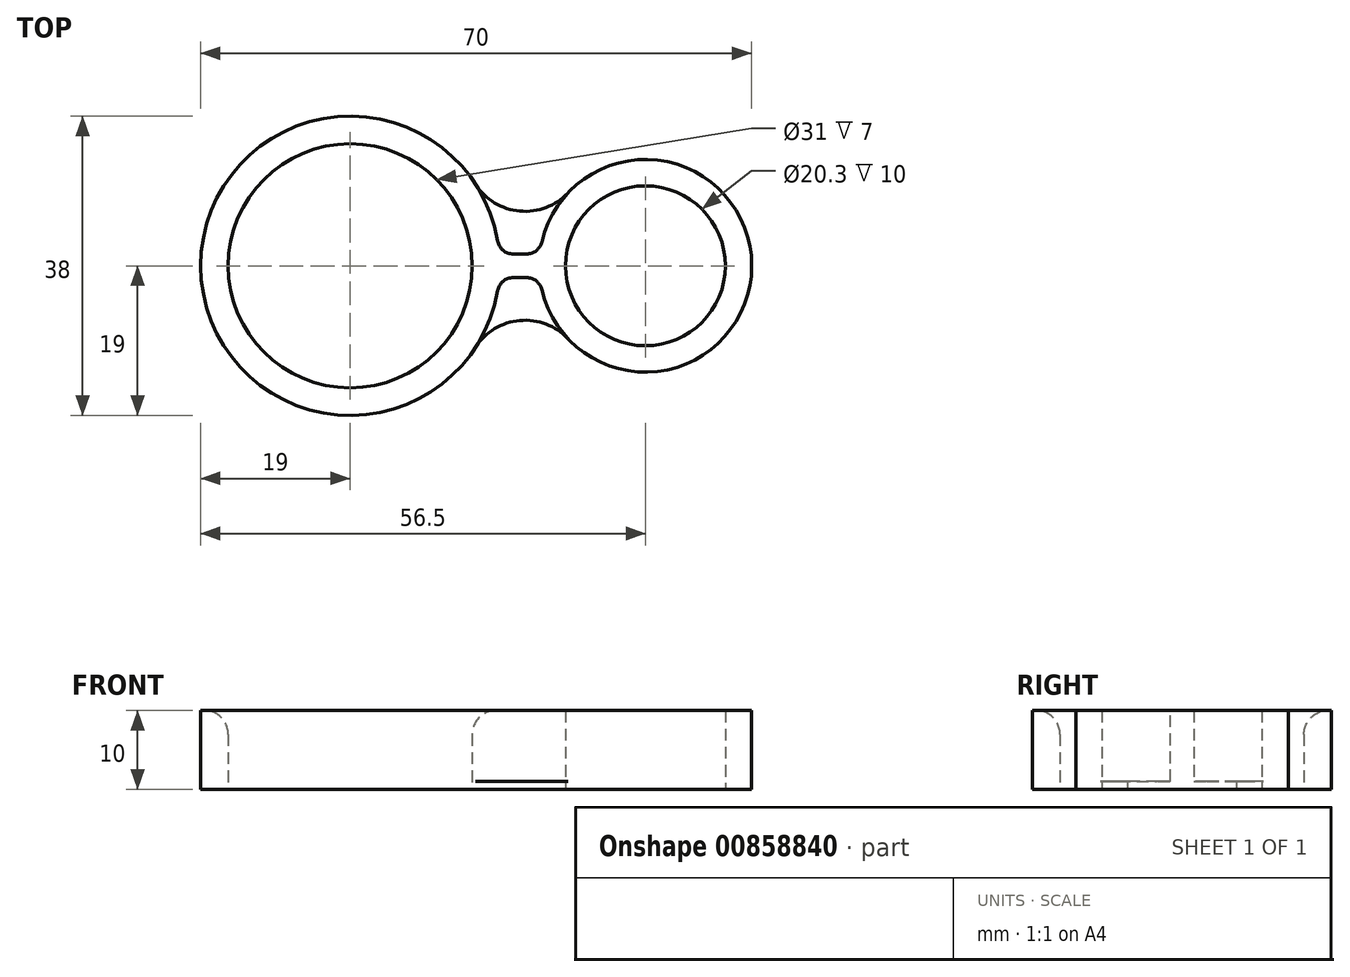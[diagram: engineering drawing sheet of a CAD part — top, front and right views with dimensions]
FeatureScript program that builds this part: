
annotation { "Feature Type Name" : "Feature", "Feature Type Description" : "" }
export const myFeature = defineFeature(function(context is Context, id is Id, definition is map)
    precondition{}
    {
        {
            var Q0;
            Q0=qCreatedBy(makeId("Top.planeOp"),FACE);
            var sketch = newSketch(context, id + "F0", { "sketchPlane" : qUnion([Q0])});
            skCircle(sketch, "E0", {"center": v(0, 0) * mm, "radius": 15.5 * mm});
            skLineSegment(sketch, "E1", {"start": v(37.5, 37.08) * mm, "end": v(37.5, -39.04) * mm, "construction": true});
            skLineSegment(sketch, "E2", {"start": v(-74.97, 0) * mm, "end": v(75.92, 0) * mm, "construction": true});
            skCircle(sketch, "E3", {"center": v(37.5, 0) * mm, "radius": 10.15 * mm});
            skCircle(sketch, "E4", {"center": v(0, 0) * mm, "radius": 19 * mm});
            skCircle(sketch, "E5", {"center": v(37.5, 0) * mm, "radius": 13.5 * mm});
            skArc(sketch, "E6", {"start": v(27.69, -9.27) * mm, "mid": v(21.55, -6.95) * mm, "end": v(15.94, -10.34) * mm});
            skArc(sketch, "E7", {"start": v(15.94, 10.34) * mm, "mid": v(21.55, 6.95) * mm, "end": v(27.69, 9.27) * mm});
            skLineSegment(sketch, "E8.trimOffspring", {"start": v(18.94, -1.5) * mm, "end": v(24.08, -1.5) * mm});
            skLineSegment(sketch, "E9.MirrorCS", {"start": v(18.94, 1.5) * mm, "end": v(24.08, 1.5) * mm});
            skSolve(sketch);
        }
        {
            var Q0;
            Q0=makeQuery(id+"F0.imprint","IMPRINT",FACE,{"disambiguationData":[TD([[makeQuery(id+"F0.imprint","IMPRINT",EDGE,{"derivedFrom":sQuery(id+"F0.wireOp",EDGE,"E0")}),-1.0]])]});
            var Q1;
            {var subQ0=sQuery(id+"F0.wireOp",EDGE,"E8.trimOffspring");Q1=makeQuery(id+"F0.imprint","IMPRINT",FACE,{"disambiguationData":[TD([[makeQuery(id+"F0.imprint","IMPRINT",EDGE,{"derivedFrom":subQ0}),1.0]])]});}
            var Q2;
            Q2=makeQuery(id+"F0.imprint","IMPRINT",FACE,{"disambiguationData":[TD([[makeQuery(id+"F0.imprint","IMPRINT",EDGE,{"derivedFrom":sQuery(id+"F0.wireOp",EDGE,"E3")}),-1.0]])]});
            extrude(context, id + "F1", {"entities" : qUnion([Q0, Q1, Q2]), "depth" : 10 * mm, "offsetDistance" : 25 * mm});
        }
        {
            var Q0;
            {var subQ0=sQuery(id+"F0.wireOp",EDGE,"E7");Q0=makeQuery(id+"F0.imprint","IMPRINT",FACE,{"disambiguationData":[TD([[makeQuery(id+"F0.imprint","IMPRINT",EDGE,{"derivedFrom":subQ0}),-1.0]])]});}
            var Q1;
            {var subQ0=sQuery(id+"F0.wireOp",EDGE,"E6");Q1=makeQuery(id+"F0.imprint","IMPRINT",FACE,{"disambiguationData":[TD([[makeQuery(id+"F0.imprint","IMPRINT",EDGE,{"derivedFrom":subQ0}),-1.0]])]});}
            extrude(context, id + "F2", {"entities" : qUnion([Q0, Q1]), "operationType" : NewBodyOperationType.ADD, "depth" : 1 * mm, "offsetDistance" : 25 * mm});
        }
        {
            var Q0;
            Q0=makeQuery(id+"F1.opExtrude","CAP_EDGE",EDGE,{"disambiguationData":[OSD([sQuery(id+"F0.wireOp",EDGE,"E0")])],"isStart":false});
            fillet(context, id + "F3", {"entities" : qUnion([Q0]), "radius" : 3 * mm, "tangentPropagation" : true, "allowEdgeOverflow" : false});
        }
        {
            var Q0;
            {var subQ0=sQuery(id+"F0.wireOp",EDGE,"E4");Q0=makeQuery(id+"F2.opExtrude","CAP_EDGE",EDGE,{"disambiguationData":[OSD([subQ0]),TDD([makeQuery(id+"F0.imprint","IMPRINT",EDGE,{"disambiguationData":[TD([[makeQuery(id+"F0.imprint","INTERSECT",VERTEX,{"derivedFrom":[subQ0,sQuery(id+"F0.wireOp",EDGE,"E6")]}),-1.0]])],"derivedFrom":subQ0})])],"isStart":false});}
            var Q1;
            Q1=makeQuery(id+"F2.opExtrude","CAP_EDGE",EDGE,{"disambiguationData":[OSD([sQuery(id+"F0.wireOp",EDGE,"E8.trimOffspring")])],"isStart":false});
            var Q2;
            {var subQ0=sQuery(id+"F0.wireOp",EDGE,"E5");Q2=makeQuery(id+"F2.opExtrude","CAP_EDGE",EDGE,{"disambiguationData":[OSD([subQ0]),TDD([makeQuery(id+"F0.imprint","IMPRINT",EDGE,{"disambiguationData":[TD([[makeQuery(id+"F0.imprint","INTERSECT",VERTEX,{"derivedFrom":[subQ0,sQuery(id+"F0.wireOp",EDGE,"E6")]}),1.0]])],"derivedFrom":subQ0})])],"isStart":false});}
            var Q3;
            Q3=makeQuery(id+"F1.opExtrude","SWEPT_EDGE",EDGE,{"disambiguationData":[OSD([sQuery(id+"F0.wireOp",EDGE,"E4"),sQuery(id+"F0.wireOp",EDGE,"E8.trimOffspring")])]});
            var Q4;
            Q4=makeQuery(id+"F1.opExtrude","SWEPT_EDGE",EDGE,{"disambiguationData":[OSD([sQuery(id+"F0.wireOp",EDGE,"E5"),sQuery(id+"F0.wireOp",EDGE,"E8.trimOffspring")])]});
            var Q5;
            Q5=makeQuery(id+"F1.opExtrude","SWEPT_EDGE",EDGE,{"disambiguationData":[OSD([sQuery(id+"F0.wireOp",EDGE,"E5"),sQuery(id+"F0.wireOp",EDGE,"E9.MirrorCS")])]});
            var Q6;
            Q6=makeQuery(id+"F1.opExtrude","SWEPT_EDGE",EDGE,{"disambiguationData":[OSD([sQuery(id+"F0.wireOp",EDGE,"E4"),sQuery(id+"F0.wireOp",EDGE,"E9.MirrorCS")])]});
            var Q7;
            {var subQ0=sQuery(id+"F0.wireOp",EDGE,"E4");Q7=makeQuery(id+"F2.opExtrude","CAP_EDGE",EDGE,{"disambiguationData":[OSD([subQ0]),TDD([makeQuery(id+"F0.imprint","IMPRINT",EDGE,{"disambiguationData":[TD([[makeQuery(id+"F0.imprint","INTERSECT",VERTEX,{"derivedFrom":[subQ0,sQuery(id+"F0.wireOp",EDGE,"E7")]}),1.0]])],"derivedFrom":subQ0})])],"isStart":false});}
            var Q8;
            {var subQ0=sQuery(id+"F0.wireOp",EDGE,"E5");Q8=makeQuery(id+"F2.opExtrude","CAP_EDGE",EDGE,{"disambiguationData":[OSD([subQ0]),TDD([makeQuery(id+"F0.imprint","IMPRINT",EDGE,{"disambiguationData":[TD([[makeQuery(id+"F0.imprint","INTERSECT",VERTEX,{"derivedFrom":[subQ0,sQuery(id+"F0.wireOp",EDGE,"E7")]}),-1.0]])],"derivedFrom":subQ0})])],"isStart":false});}
            var Q9;
            Q9=makeQuery(id+"F2.opExtrude","CAP_EDGE",EDGE,{"disambiguationData":[OSD([sQuery(id+"F0.wireOp",EDGE,"E9.MirrorCS")])],"isStart":false});
            fillet(context, id + "F4", {"entities" : qUnion([Q0, Q1, Q2, Q3, Q4, Q5, Q6, Q7, Q8, Q9]), "radius" : 2 * mm, "tangentPropagation" : true, "allowEdgeOverflow" : false});
        }
    });
